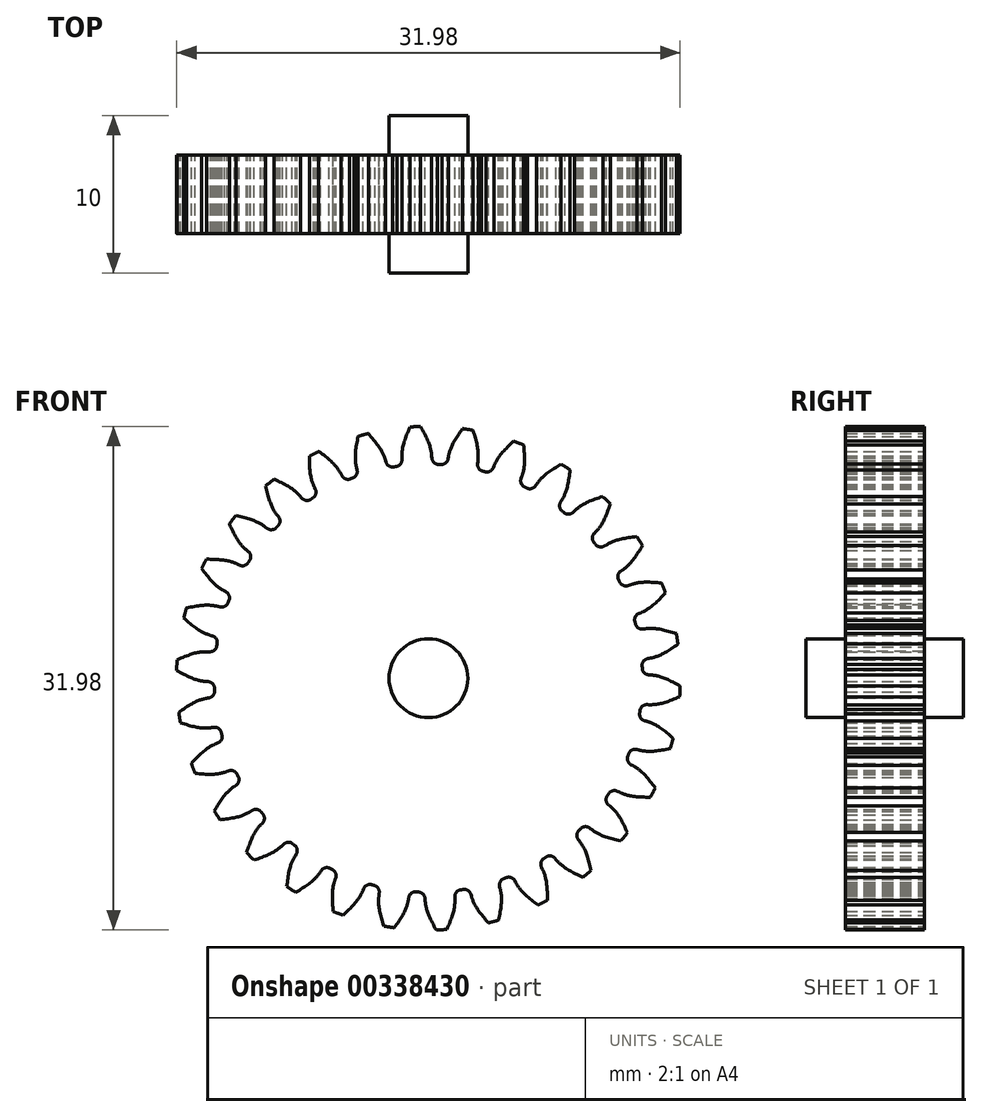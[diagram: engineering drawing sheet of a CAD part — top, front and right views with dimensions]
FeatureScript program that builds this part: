
annotation { "Feature Type Name" : "Feature", "Feature Type Description" : "" }
export const myFeature = defineFeature(function(context is Context, id is Id, definition is map)
    precondition{}
    {
        {
            assignVariable(context, id + "F0", {"name" : "N", "anyValue" : 30});
        }
        {
            assignVariable(context, id + "F1", {"name" : "WoF", "anyValue" : 5});
        }
        {
            var Q0;
            Q0=qCreatedBy(makeId("Front.planeOp"),FACE);
            var sketch = newSketch(context, id + "F2", { "sketchPlane" : qUnion([Q0])});
            skCircle(sketch, "E0", {"center": v(0, 0) * mm, "radius": 13.6 * mm});
            skSolve(sketch);
        }
        {
            var Q0;
            Q0=qSketchRegion(id+"F2",true);
            extrude(context, id + "F3", {"entities" : qUnion([Q0]), "endBound" : BoundingType.SYMMETRIC, "depth" : (getVariable(context, 'WoF')) * mm});
        }
        {
            var Q0;
            Q0=qCreatedBy(makeId("Front.planeOp"),FACE);
            var sketch = newSketch(context, id + "F4", { "sketchPlane" : qUnion([Q0])});
            skCircle(sketch, "E1", {"center": v(0, 0) * mm, "radius": 15 * mm, "construction": true});
            skCircle(sketch, "E2", {"center": v(0, 0) * mm, "radius": 16 * mm, "construction": true});
            skLineSegment(sketch, "E3", {"start": v(0, 0) * mm, "end": v(0, 15) * mm, "construction": true});
            skPoint(sketch, "E4", {"position": v(0, 15) * mm});
            skLineSegment(sketch, "E5", {"start": v(-4.82, 13.25) * mm, "end": v(0, 0) * mm, "construction": true});
            skArc(sketch, "E6", {"start": v(-4.82, 13.25) * mm, "mid": v(-3.68, 13.6) * mm, "end": v(-2.5, 13.87) * mm, "construction": true});
            skArc(sketch, "E7", {"start": v(-4.82, 13.25) * mm, "mid": v(-6.47, 12.52) * mm, "end": v(-8.01, 11.6) * mm, "construction": true});
            skArc(sketch, "E8", {"start": v(-2.5, 13.87) * mm, "mid": v(-1.15, 14.05) * mm, "end": v(0.21, 14.1) * mm, "construction": true});
            skLineSegment(sketch, "E9", {"start": v(0, 15) * mm, "end": v(0, 16) * mm, "construction": true});
            skLineSegment(sketch, "E10", {"start": v(0, 15) * mm, "end": v(-4.82, 13.25) * mm, "construction": true});
            skLineSegment(sketch, "E11", {"start": v(0, 15) * mm, "end": v(-5.57, 15) * mm, "construction": true});
            skLineSegment(sketch, "E12", {"start": v(-8.01, 11.6) * mm, "end": v(-0.83, 16.56) * mm, "construction": true});
            skLineSegment(sketch, "E13", {"start": v(-2.5, 13.87) * mm, "end": v(0.18, 14.36) * mm, "construction": true});
            skLineSegment(sketch, "E14", {"start": v(0, 0) * mm, "end": v(-0.84, 15.98) * mm, "construction": true});
            skCircle(sketch, "E15", {"center": v(0, 0) * mm, "radius": 13.6 * mm, "construction": true});
            skLineSegment(sketch, "E16", {"start": v(0, 0) * mm, "end": v(0.71, 13.58) * mm, "construction": true});
            skPoint(sketch, "E17", {"position": v(0.21, 14.1) * mm});
            skPoint(sketch, "E18", {"position": v(0.18, 14.36) * mm});
            skPoint(sketch, "E19", {"position": v(-0.83, 16.56) * mm});
            skPoint(sketch, "E20", {"position": v(-0.84, 15.98) * mm});
            skPoint(sketch, "E21", {"position": v(0.71, 13.58) * mm});
            skCircle(sketch, "E22", {"center": v(0, 0) * mm, "radius": 14 * mm, "construction": true});
            skFitSpline(sketch, "E23", {"points": [v(-0.83, 16.56) * mm, v(0, 15) * mm, v(0.18, 14.36) * mm, v(0.21, 14.1) * mm], "startDerivative": vector(1.97, -3.39) * mm, "endDerivative": vector(0.1, -1.25) * mm});
            skArc(sketch, "E24", {"start": v(-0.84, 15.98) * mm, "mid": v(-0.67, 15.99) * mm, "end": v(-0.5, 16) * mm});
            skLineSegment(sketch, "E25", {"start": v(-0.5, 16) * mm, "end": v(-0.5, 16) * mm});
            skLineSegment(sketch, "E26", {"start": v(0.21, 14.1) * mm, "end": v(0.22, 14) * mm});
            skArc(sketch, "E27", {"start": v(0.56, 13.59) * mm, "mid": v(-0.07, 13.6) * mm, "end": v(-0.71, 13.58) * mm});
            skArc(sketch, "E28", {"start": v(0.22, 14) * mm, "mid": v(0.32, 13.73) * mm, "end": v(0.56, 13.59) * mm});
            skArc(sketch, "E29.MirrorCS", {"start": v(-1.98, 13.46) * mm, "mid": v(-1.35, 13.53) * mm, "end": v(-0.71, 13.58) * mm});
            skArc(sketch, "E30.MirrorCS", {"start": v(-1.68, 13.9) * mm, "mid": v(-1.75, 13.63) * mm, "end": v(-1.98, 13.46) * mm});
            skLineSegment(sketch, "E31.MirrorCS", {"start": v(-1.68, 14) * mm, "end": v(-1.68, 13.9) * mm});
            skFitSpline(sketch, "E32.MirrorCS", {"points": [v(-0.9, 16.56) * mm, v(-1.57, 14.92) * mm, v(-1.68, 14.26) * mm, v(-1.68, 14) * mm], "startDerivative": vector(-1.6, -3.57) * mm, "endDerivative": vector(0.02, -1.25) * mm});
            skArc(sketch, "E33.MirrorCS", {"start": v(-0.84, 15.98) * mm, "mid": v(-1, 15.97) * mm, "end": v(-1.17, 15.96) * mm});
            skSolve(sketch);
        }
        {
            var Q0;
            Q0=qSketchRegion(id+"F4",true);
            var Q1;
            Q1=makeQuery(id+"F3.opExtrude","CAP_FACE",FACE,{"disambiguationData":[OSD([sQuery(id+"F2.wireOp",EDGE,"E0"),sQuery(id+"F2.wireOp",EDGE,"ypchOyP9-PMkg-Z84X-TmPn-hLIgu99tQz8k")])],"isStart":false});
            extrude(context, id + "F5", {"entities" : qUnion([Q0]), "endBound" : BoundingType.SYMMETRIC, "endBoundEntityFace" : qUnion([Q1]), "depth" : (getVariable(context, 'WoF')) * mm});
        }
        {
            var Q0;
            Q0=makeQuery(id+"F5.opExtrude","SWEPT_BODY",BODY,{"disambiguationData":[OSD([sQuery(id+"F4.wireOp",EDGE,"E23"),sQuery(id+"F4.wireOp",EDGE,"E24"),sQuery(id+"F4.wireOp",EDGE,"E26"),sQuery(id+"F4.wireOp",EDGE,"E27"),sQuery(id+"F4.wireOp",EDGE,"E28"),sQuery(id+"F4.wireOp",EDGE,"E29.MirrorCS"),sQuery(id+"F4.wireOp",EDGE,"E30.MirrorCS"),sQuery(id+"F4.wireOp",EDGE,"E31.MirrorCS"),sQuery(id+"F4.wireOp",EDGE,"E32.MirrorCS"),sQuery(id+"F4.wireOp",EDGE,"E33.MirrorCS")])]});
            var Q1;
            Q1=makeQuery(id+"F3.opExtrude","CAP_EDGE",EDGE,{"disambiguationData":[OSD([sQuery(id+"F2.wireOp",EDGE,"E0")])],"isStart":false});
            circularPattern(context, id + "F6", {"operationType" : NewBodyOperationType.ADD, "entities" : qUnion([Q0]), "axis" : qUnion([Q1]), "angle" : 360 * degree, "instanceCount" : getVariable(context, 'N'), "equalSpace" : true});
        }
        {
            var Q0;
            Q0=qCreatedBy(makeId("Front.planeOp"),FACE);
            var sketch = newSketch(context, id + "F7", { "sketchPlane" : qUnion([Q0])});
            skCircle(sketch, "E34", {"center": v(0, 0) * mm, "radius": 2.5 * mm});
            skSolve(sketch);
        }
        {
            var Q0;
            Q0 = qSketchRegion(id + "F7", true);
            extrude(context, id + "F8", {"entities" : qUnion([Q0]), "operationType" : NewBodyOperationType.ADD, "endBound" : BoundingType.SYMMETRIC, "depth" : 10 * mm});
        }
    });
